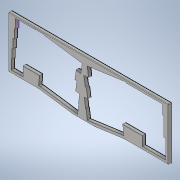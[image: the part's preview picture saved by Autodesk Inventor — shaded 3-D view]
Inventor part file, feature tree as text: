
AUTODESK INVENTOR PART (.ipt)
format: ipt  version: 2022 (Build 260153000, 153)  size: 293,376 bytes
history: mixed  units: in
note: dims shown in document units (in); Inventor stores cm internally (conversion verified against a paired STEP export)
features: fillet x1, sketch x1, imported_body x1
ambient origin geometry x8: Origin, YZ Plane, XZ Plane, XY Plane, X Axis, Y Axis, Z Axis, Center Point
bodies: Solid1 (imported_parasolid), Body3 (imported_parasolid), Solid2 (imported_parasolid)
feature tree (3):
  fillet  "Fillet1"  Radius=0.0394in
  sketch  "Sketch1"
  imported_body  NMx_Import_Brep_tag  [imported B-rep: ~58 faces, bbox_mm=[317.227862, 115.578317, 6.35]]
